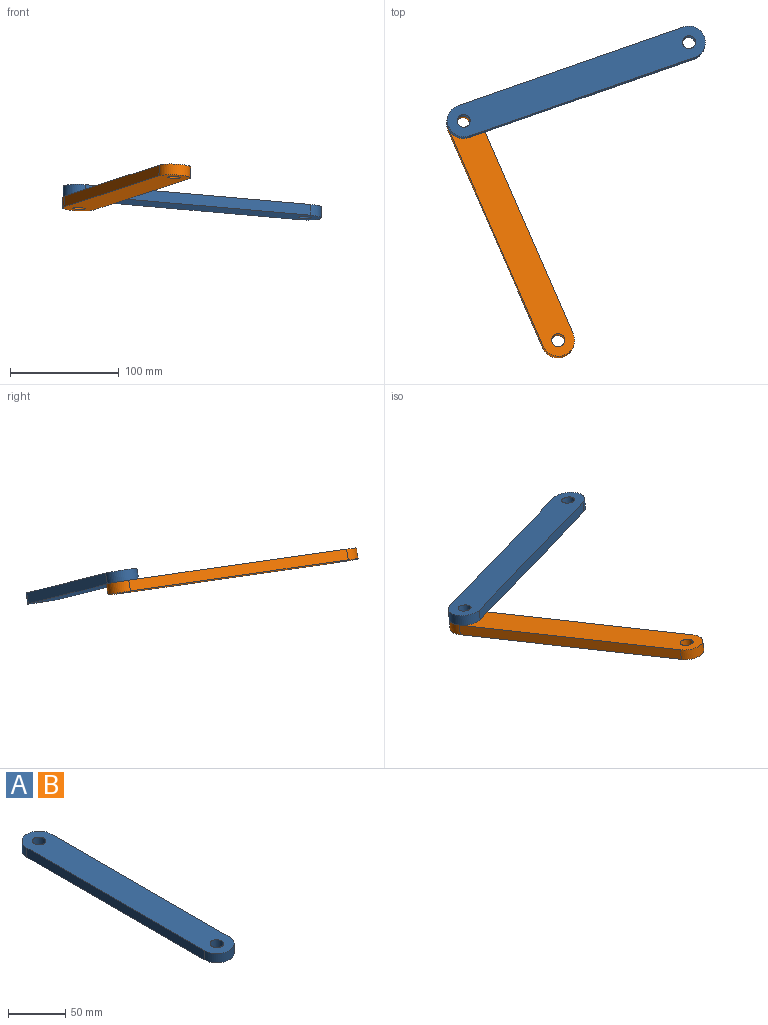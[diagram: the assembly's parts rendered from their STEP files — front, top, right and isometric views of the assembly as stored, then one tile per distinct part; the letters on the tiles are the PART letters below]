
ASSEMBLY  parts=2 mates=1
PART A: 8 faces, bbox 30x250x10 mm
  f0: plane 220x10mm, normal (1,0,0), area 2200mm2, adj f1,f3,f6,f7
  f1: plane 250x30mm, normal (0,0,1), area 7080.7mm2, adj f0,f2,f4,f5,f6,f7
  f2: plane 220x10mm, normal (-1,0,0), area 2200mm2, adj f1,f3,f6,f7
  f3: plane 250x30mm, normal (0,0,-1), area 7080.7mm2, adj f0,f2,f4,f5,f6,f7
  f4: cylinder r=6mm len=12mm, axis (0,0,1), area 377mm2, adj f1,f3
  f5: cylinder r=6mm len=12mm, axis (0,0,1), area 377mm2, adj f1,f3
  f6: cylinder r=15mm len=30mm, axis (0,0,1), area 471.2mm2, adj f0,f1,f2,f3
  f7: cylinder r=15mm len=30mm, axis (0,0,-1), area 471.2mm2, adj f0,f1,f2,f3
PART B: same geometry as A
PLACE A rot(axis=(-0.13,-0.05,-0.99),71deg) t=(80.69,238.21,-20.24)mm
PLACE B rot(axis=(-0.03,-0.07,-1),156.9deg) t=(165.8,221.68,-30.57)mm
MATE revolute A.f6 <-> B.f6  axis (0.03,0.16,0.99) through (115.96,187.65,-1.04)mm
